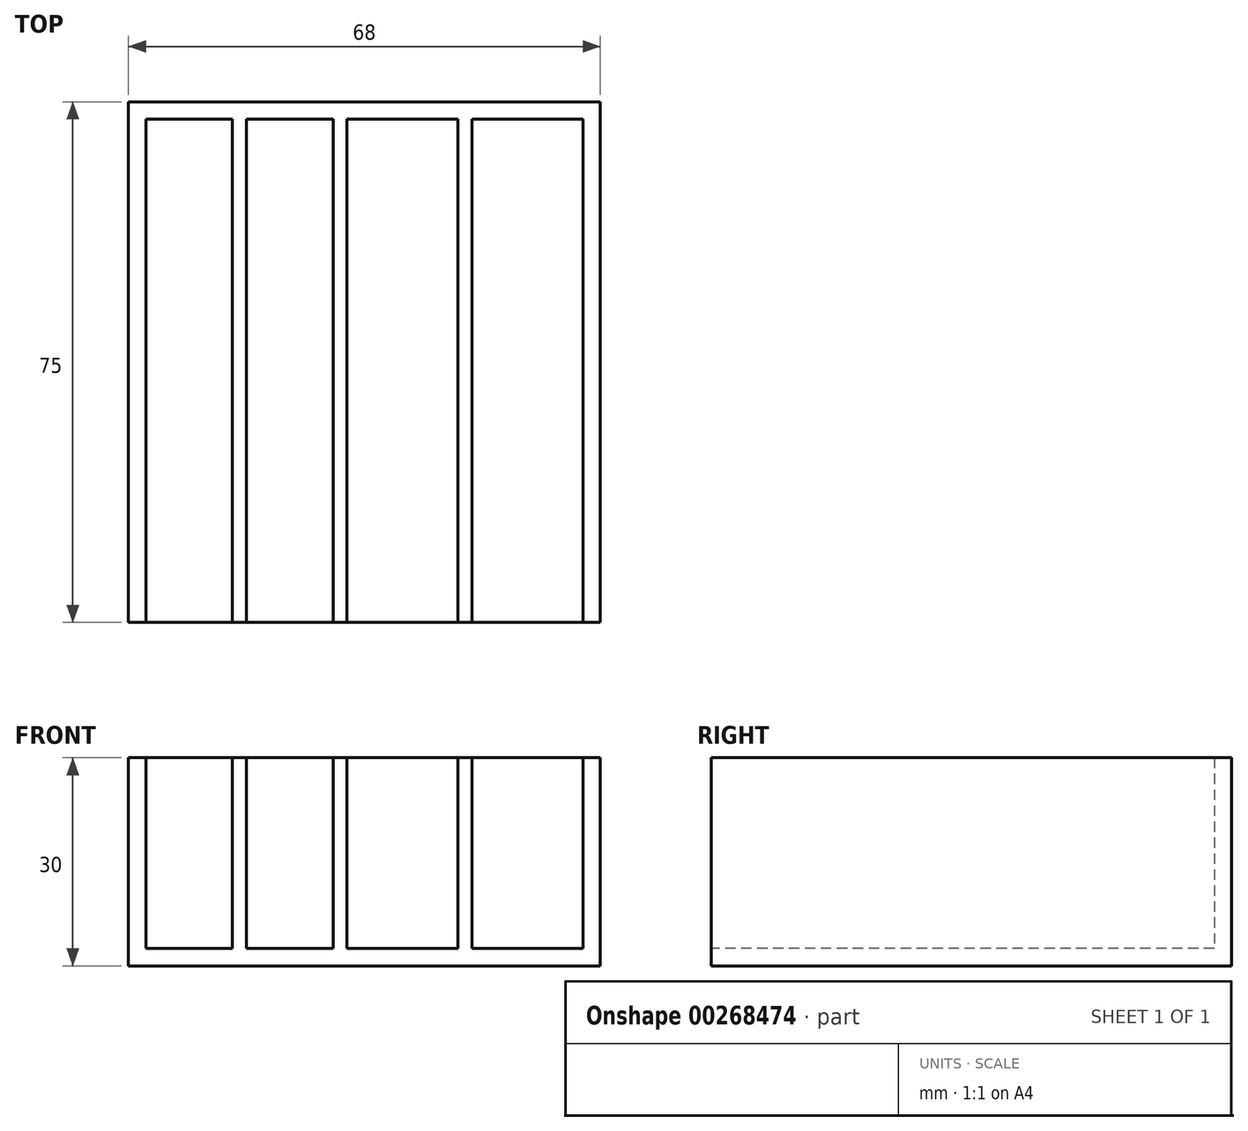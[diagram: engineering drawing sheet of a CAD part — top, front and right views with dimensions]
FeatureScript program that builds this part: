
annotation { "Feature Type Name" : "Feature", "Feature Type Description" : "" }
export const myFeature = defineFeature(function(context is Context, id is Id, definition is map)
    precondition{}
    {
        {
            var Q0;
            Q0=qCreatedBy(makeId("Top.planeOp"),FACE);
            var sketch = newSketch(context, id + "F0", { "sketchPlane" : qUnion([Q0])});
            skPoint(sketch, "E0.middle", {"position": v(0, 0) * mm});
            skLineSegment(sketch, "E1.bottom", {"start": v(34, -37.5) * mm, "end": v(-34, -37.5) * mm});
            skLineSegment(sketch, "E1.top", {"start": v(34, 37.5) * mm, "end": v(-34, 37.5) * mm});
            skLineSegment(sketch, "E1.left", {"start": v(34, -37.5) * mm, "end": v(34, 37.5) * mm});
            skLineSegment(sketch, "E1.right", {"start": v(-34, -37.5) * mm, "end": v(-34, 37.5) * mm});
            skSolve(sketch);
        }
        {
            var Q0;
            Q0 = qSketchRegion(id + "F0", true);
            extrude(context, id + "F1", {"entities" : qUnion([Q0]), "depth" : 2.5 * mm, "offsetDistance" : 25 * mm});
        }
        {
            var Q0;
            Q0=makeQuery(id+"F1.opExtrude","CAP_FACE",FACE,{"disambiguationData":[OSD([sQuery(id+"F0.wireOp",EDGE,"E1.bottom"),sQuery(id+"F0.wireOp",EDGE,"E1.top"),sQuery(id+"F0.wireOp",EDGE,"E1.left"),sQuery(id+"F0.wireOp",EDGE,"E1.right")])],"isStart":false});
            var sketch = newSketch(context, id + "F2", { "sketchPlane" : qUnion([Q0])});
            skLineSegment(sketch, "E2.bottom", {"start": v(-34, 37.5) * mm, "end": v(-31.5, 37.5) * mm});
            skLineSegment(sketch, "E2.top", {"start": v(-34, -37.5) * mm, "end": v(-31.5, -37.5) * mm});
            skLineSegment(sketch, "E2.left", {"start": v(-34, 37.5) * mm, "end": v(-34, -37.5) * mm});
            skLineSegment(sketch, "E2.right", {"start": v(-31.5, 37.5) * mm, "end": v(-31.5, -37.5) * mm});
            skLineSegment(sketch, "E3.bottom", {"start": v(-19, 37.5) * mm, "end": v(-17, 37.5) * mm});
            skLineSegment(sketch, "E3.top", {"start": v(-19, -37.5) * mm, "end": v(-17, -37.5) * mm});
            skLineSegment(sketch, "E3.left", {"start": v(-19, 37.5) * mm, "end": v(-19, -37.5) * mm});
            skLineSegment(sketch, "E3.right", {"start": v(-17, 37.5) * mm, "end": v(-17, -37.5) * mm});
            skLineSegment(sketch, "E4.bottom", {"start": v(-4.5, 37.5) * mm, "end": v(-2.5, 37.5) * mm});
            skLineSegment(sketch, "E4.top", {"start": v(-4.5, -37.5) * mm, "end": v(-2.5, -37.5) * mm});
            skLineSegment(sketch, "E4.left", {"start": v(-4.5, 37.5) * mm, "end": v(-4.5, -37.5) * mm});
            skLineSegment(sketch, "E4.right", {"start": v(-2.5, 37.5) * mm, "end": v(-2.5, -37.5) * mm});
            skLineSegment(sketch, "E5.bottom", {"start": v(13.5, 37.5) * mm, "end": v(15.5, 37.5) * mm});
            skLineSegment(sketch, "E5.top", {"start": v(13.5, -37.5) * mm, "end": v(15.5, -37.5) * mm});
            skLineSegment(sketch, "E5.left", {"start": v(13.5, 37.5) * mm, "end": v(13.5, -37.5) * mm});
            skLineSegment(sketch, "E5.right", {"start": v(15.5, 37.5) * mm, "end": v(15.5, -37.5) * mm});
            skLineSegment(sketch, "E6.bottom", {"start": v(34, 37.5) * mm, "end": v(31.5, 37.5) * mm});
            skLineSegment(sketch, "E6.top", {"start": v(34, -37.5) * mm, "end": v(31.5, -37.5) * mm});
            skLineSegment(sketch, "E6.left", {"start": v(34, 37.5) * mm, "end": v(34, -37.5) * mm});
            skLineSegment(sketch, "E6.right", {"start": v(31.5, 37.5) * mm, "end": v(31.5, -37.5) * mm});
            skLineSegment(sketch, "E7.bottom", {"start": v(-34, 37.5) * mm, "end": v(34, 37.5) * mm});
            skLineSegment(sketch, "E7.top", {"start": v(-34, 35) * mm, "end": v(34, 35) * mm});
            skLineSegment(sketch, "E7.left", {"start": v(-34, 37.5) * mm, "end": v(-34, 35) * mm});
            skLineSegment(sketch, "E7.right", {"start": v(34, 37.5) * mm, "end": v(34, 35) * mm});
            skSolve(sketch);
        }
        {
            var Q0;
            Q0 = qSketchRegion(id + "F2", true);
            extrude(context, id + "F3", {"entities" : qUnion([Q0]), "operationType" : NewBodyOperationType.ADD, "depth" : 27.5 * mm, "offsetDistance" : 25 * mm});
        }
    });
